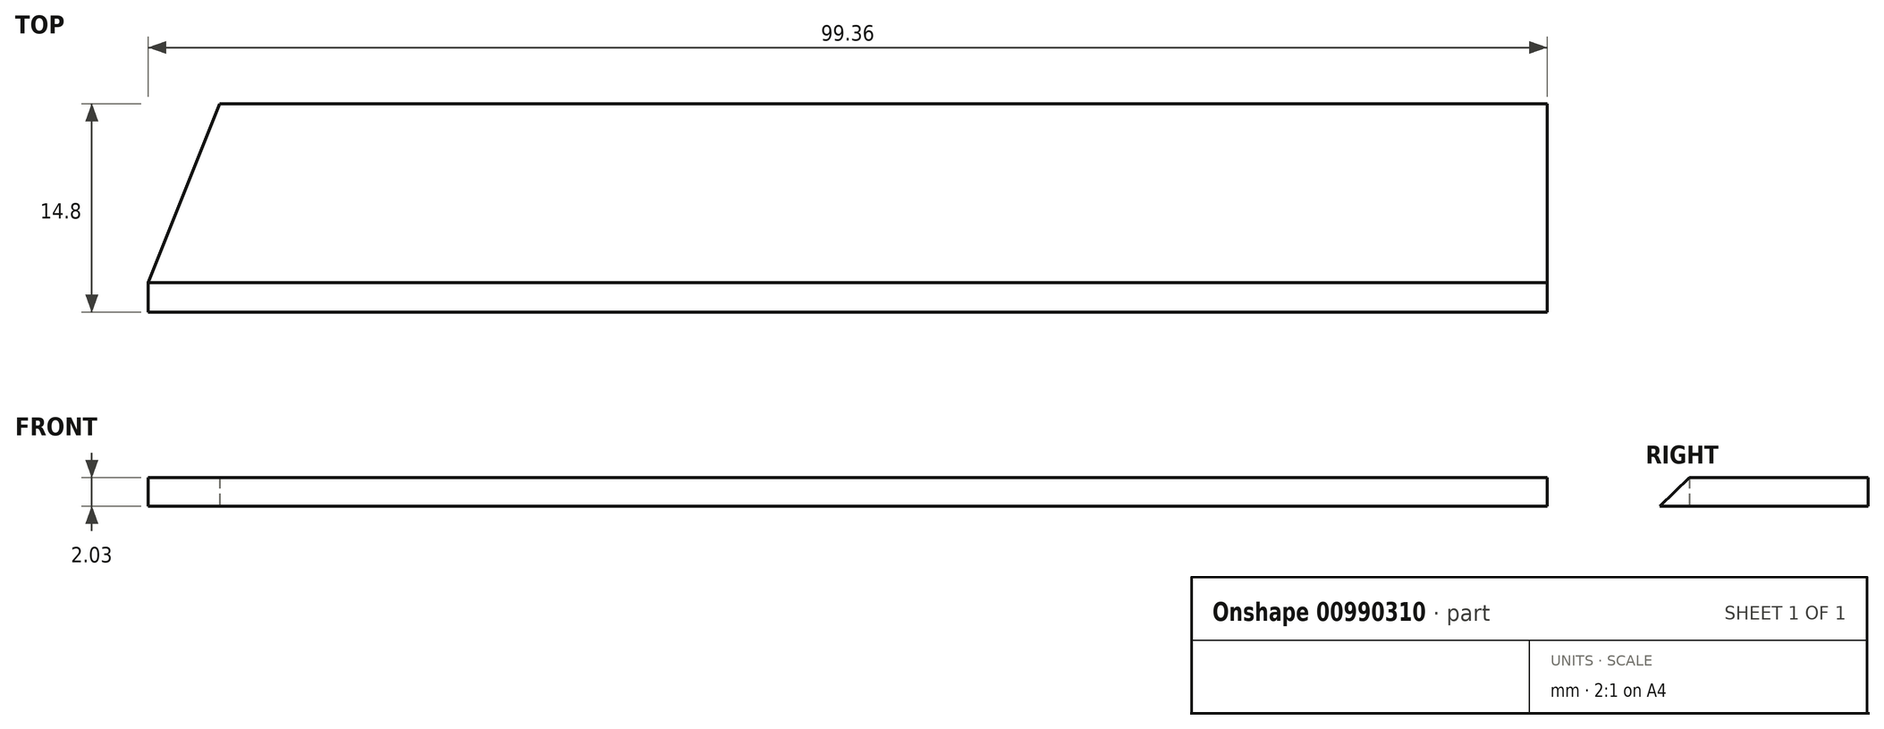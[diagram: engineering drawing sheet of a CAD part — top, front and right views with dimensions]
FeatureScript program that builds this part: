
annotation { "Feature Type Name" : "Feature", "Feature Type Description" : "" }
export const myFeature = defineFeature(function(context is Context, id is Id, definition is map)
    precondition{}
    {
        {
            var Q0;
            Q0=qCreatedBy(makeId("Top.planeOp"),FACE);
            var sketch = newSketch(context, id + "F0", { "sketchPlane" : qUnion([Q0])});
            skLineSegment(sketch, "E0.bottom", {"start": v(49.68, 6.35) * mm, "end": v(-44.6, 6.35) * mm});
            skLineSegment(sketch, "E0.top", {"start": v(49.68, -6.35) * mm, "end": v(-49.68, -6.35) * mm});
            skLineSegment(sketch, "E0.left", {"start": v(49.68, 6.35) * mm, "end": v(49.68, -6.35) * mm});
            skPoint(sketch, "E0.middle", {"position": v(0, 0) * mm});
            skLineSegment(sketch, "E1", {"start": v(-49.68, -6.35) * mm, "end": v(-44.6, 6.35) * mm});
            skPoint(sketch, "E0.right.start.orphan", {"position": v(-49.68, 6.35) * mm});
            skLineSegment(sketch, "E2", {"start": v(-44.6, 6.35) * mm, "end": v(-44.6, -6.35) * mm, "construction": true});
            skSolve(sketch);
        }
        {
            var Q0;
            Q0=makeQuery(id+"F0.imprint","IMPRINT",FACE,{"disambiguationData":[TD([[makeQuery(id+"F0.imprint","IMPRINT",EDGE,{"derivedFrom":sQuery(id+"F0.wireOp",EDGE,"E0.bottom")}),1.0]])]});
            extrude(context, id + "F1", {"entities" : qUnion([Q0]), "depth" : 2.03 * mm, "offsetDistance" : 25.4 * mm});
        }
        {
            var Q0;
            Q0=makeQuery(id+"F1.opExtrude","SWEPT_FACE",FACE,{"disambiguationData":[OSD([sQuery(id+"F0.wireOp",EDGE,"E0.left")])]});
            var sketch = newSketch(context, id + "F2", { "sketchPlane" : qUnion([Q0])});
            skLineSegment(sketch, "E3", {"start": v(-6.35, 2.03) * mm, "end": v(-8.45, 0) * mm});
            skLineSegment(sketch, "E4", {"start": v(-8.45, 0) * mm, "end": v(-6.35, 0) * mm});
            skSolve(sketch);
        }
        {
            var Q0;
            Q0=makeQuery(id+"F2.imprint","IMPRINT",FACE,{"disambiguationData":[TD([[makeQuery(id+"F2.imprint","IMPRINT",EDGE,{"derivedFrom":sQuery(id+"F2.wireOp",EDGE,"E3")}),1.0]])]});
            var Q1;
            Q1=makeQuery(id+"F1.opExtrude","CAP_VERTEX",VERTEX,{"disambiguationData":[OSD([sQuery(id+"F0.wireOp",EDGE,"E0.top"),sQuery(id+"F0.wireOp",EDGE,"E1")])],"isStart":true});
            extrude(context, id + "F3", {"entities" : qUnion([Q0]), "operationType" : NewBodyOperationType.ADD, "endBound" : BoundingType.UP_TO_VERTEX, "oppositeDirection" : true, "depth" : 25.4 * mm, "endBoundEntityVertex" : qUnion([Q1]), "offsetDistance" : 25.4 * mm});
        }
    });
